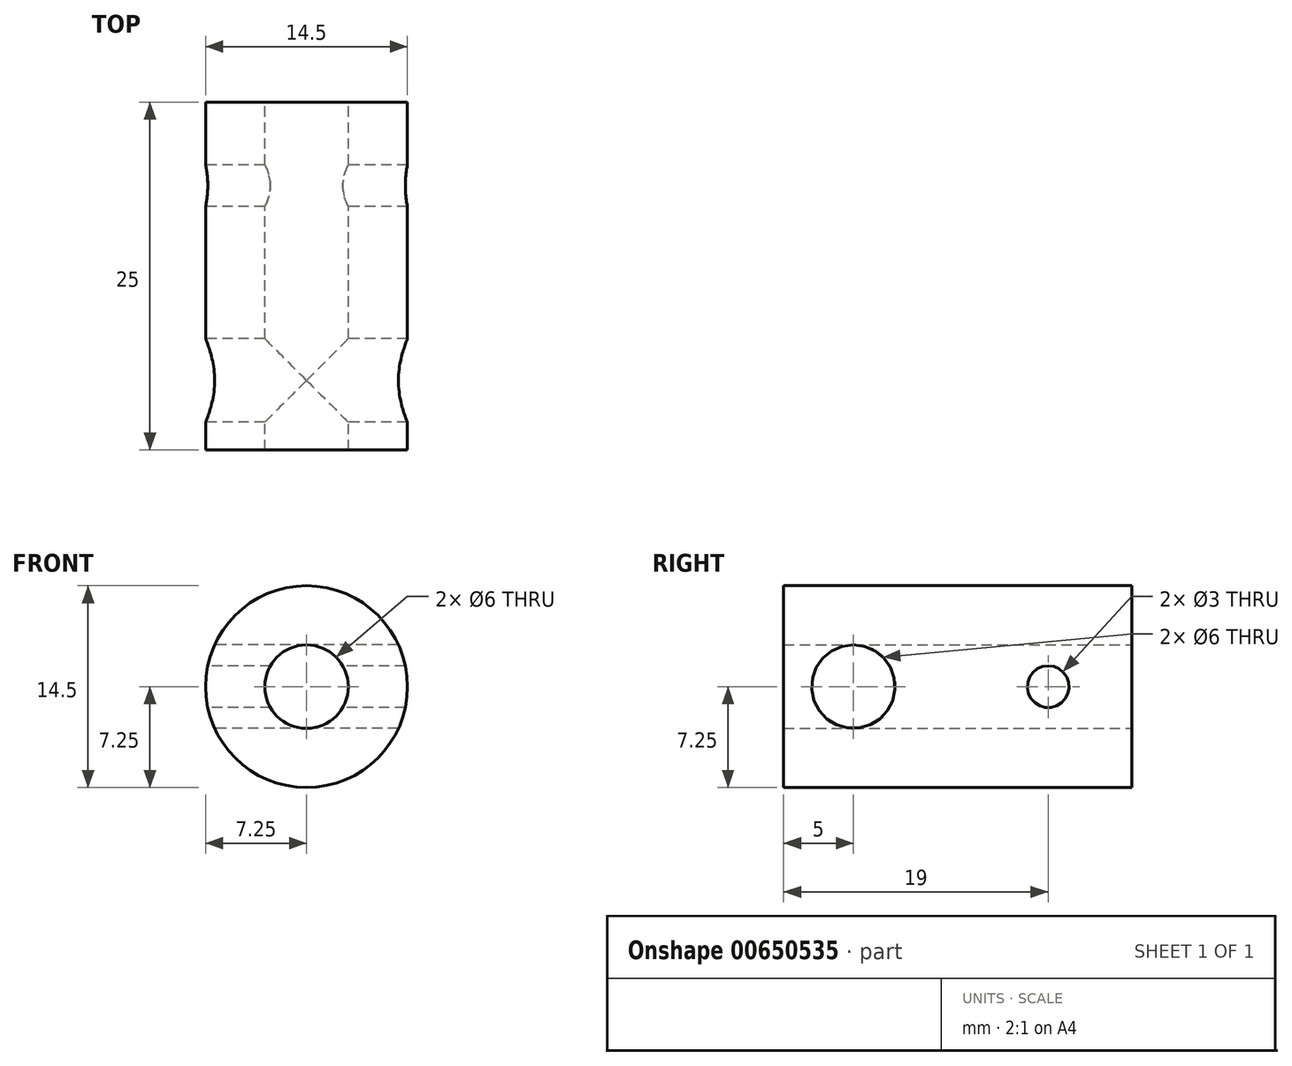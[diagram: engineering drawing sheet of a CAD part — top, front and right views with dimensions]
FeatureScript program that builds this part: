
annotation { "Feature Type Name" : "Feature", "Feature Type Description" : "" }
export const myFeature = defineFeature(function(context is Context, id is Id, definition is map)
    precondition{}
    {
        {
            var Q0;
            Q0=qCreatedBy(makeId("Front.planeOp"),FACE);
            var sketch = newSketch(context, id + "F0", { "sketchPlane" : qUnion([Q0])});
            skCircle(sketch, "E0", {"center": v(0, 0) * mm, "radius": 3 * mm});
            skCircle(sketch, "E1", {"center": v(0, 0) * mm, "radius": 7.25 * mm});
            skSolve(sketch);
        }
        {
            var Q0;
            Q0=makeQuery(id+"F0.imprint","IMPRINT",FACE,{"disambiguationData":[TD([[makeQuery(id+"F0.imprint","IMPRINT",EDGE,{"derivedFrom":sQuery(id+"F0.wireOp",EDGE,"E0")}),-1.0]])]});
            extrude(context, id + "F1", {"entities" : qUnion([Q0]), "depth" : 25 * mm, "offsetDistance" : 25 * mm});
        }
        {
            var Q0;
            Q0=qCreatedBy(makeId("Right.planeOp"),FACE);
            var sketch = newSketch(context, id + "F2", { "sketchPlane" : qUnion([Q0])});
            skCircle(sketch, "E2", {"center": v(-20, 0) * mm, "radius": 3 * mm});
            skCircle(sketch, "E3", {"center": v(-6, 0) * mm, "radius": 1.5 * mm});
            skSolve(sketch);
        }
        {
            var Q0;
            Q0 = qSketchRegion(id + "F2", true);
            extrude(context, id + "F3", {"entities" : qUnion([Q0]), "operationType" : NewBodyOperationType.REMOVE, "endBound" : BoundingType.THROUGH_ALL, "depth" : 25 * mm, "offsetDistance" : 25 * mm, "hasSecondDirection" : true, "secondDirectionBound" : SecondDirectionBoundingType.THROUGH_ALL, "secondDirectionOppositeDirection" : true, "secondDirectionDepth" : 25 * mm});
        }
    });
